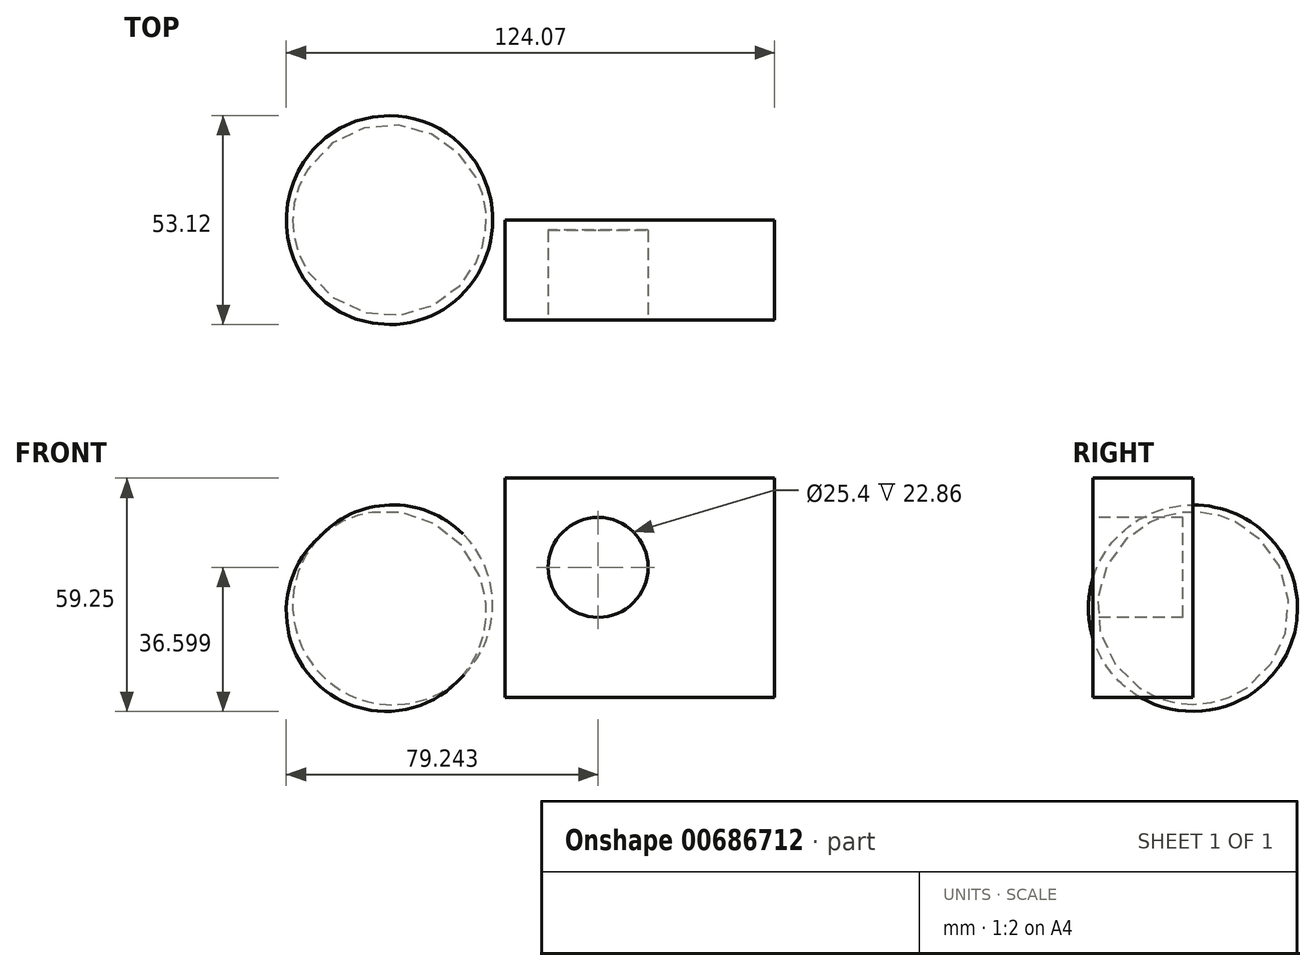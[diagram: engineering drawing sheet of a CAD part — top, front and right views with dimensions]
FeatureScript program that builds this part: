
annotation { "Feature Type Name" : "Feature", "Feature Type Description" : "" }
export const myFeature = defineFeature(function(context is Context, id is Id, definition is map)
    precondition{}
    {
        {
            var Q0;
            Q0=qCreatedBy(makeId("Front.planeOp"),FACE);
            var sketch = newSketch(context, id + "F0", { "sketchPlane" : qUnion([Q0])});
            skArc(sketch, "E0", {"start": v(-7.62, -9.04) * mm, "mid": v(-8.65, 26.04) * mm, "end": v(-43.74, 26.6) * mm});
            skLineSegment(sketch, "E1", {"start": v(-43.74, 26.6) * mm, "end": v(-7.62, -9.04) * mm});
            skSolve(sketch);
        }
        {
            var Q0;
            Q0=makeQuery(id+"F0.imprint","IMPRINT",FACE,{"disambiguationData":[TD([[makeQuery(id+"F0.imprint","IMPRINT",EDGE,{"derivedFrom":sQuery(id+"F0.wireOp",EDGE,"E0")}),1.0]])]});
            var Q1;
            Q1=sQuery(id+"F0.wireOp",EDGE,"E1");
            revolve(context, id + "F1", {"entities" : qUnion([Q0]), "axis" : qUnion([Q1]), "revolveType" : RevolveType.FULL});
        }
        {
            var Q0;
            Q0=qCreatedBy(makeId("Front.planeOp"),FACE);
            var sketch = newSketch(context, id + "F2", { "sketchPlane" : qUnion([Q0])});
            skLineSegment(sketch, "E2.bottom", {"start": v(3.74, 41.81) * mm, "end": v(72.18, 41.81) * mm});
            skLineSegment(sketch, "E2.top", {"start": v(3.74, -13.86) * mm, "end": v(72.18, -13.86) * mm});
            skLineSegment(sketch, "E2.left", {"start": v(3.74, 41.81) * mm, "end": v(3.74, -13.86) * mm});
            skLineSegment(sketch, "E2.right", {"start": v(72.18, 41.81) * mm, "end": v(72.18, -13.86) * mm});
            skSolve(sketch);
        }
        {
            var Q0;
            Q0=makeQuery(id+"F2.imprint","IMPRINT",FACE,{"disambiguationData":[TD([[makeQuery(id+"F2.imprint","IMPRINT",EDGE,{"derivedFrom":sQuery(id+"F2.wireOp",EDGE,"E2.bottom")}),-1.0]])]});
            extrude(context, id + "F3", {"entities" : qUnion([Q0]), "depth" : 25.4 * mm, "offsetDistance" : 25.4 * mm});
        }
        {
            var Q0;
            Q0=makeQuery(id+"F3.opExtrude","CAP_FACE",FACE,{"disambiguationData":[OSD([sQuery(id+"F2.wireOp",EDGE,"E2.bottom"),sQuery(id+"F2.wireOp",EDGE,"E2.top"),sQuery(id+"F2.wireOp",EDGE,"E2.left"),sQuery(id+"F2.wireOp",EDGE,"E2.right")])],"isStart":false});
            var sketch = newSketch(context, id + "F4", { "sketchPlane" : qUnion([Q0])});
            skCircle(sketch, "E3", {"center": v(27.35, 19.16) * mm, "radius": 12.7 * mm});
            skSolve(sketch);
        }
        {
            var Q0;
            Q0=makeQuery(id+"F4.imprint","IMPRINT",FACE,{"disambiguationData":[TD([[makeQuery(id+"F4.imprint","IMPRINT",EDGE,{"derivedFrom":sQuery(id+"F4.wireOp",EDGE,"E3")}),1.0]])]});
            extrude(context, id + "F5", {"entities" : qUnion([Q0]), "operationType" : NewBodyOperationType.REMOVE, "oppositeDirection" : true, "depth" : 22.86 * mm, "offsetDistance" : 25.4 * mm});
        }
    });
